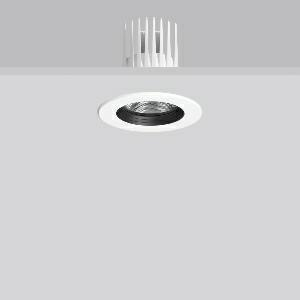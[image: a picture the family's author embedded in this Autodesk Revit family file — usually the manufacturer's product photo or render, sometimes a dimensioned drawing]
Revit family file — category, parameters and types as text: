
# Revit family: heledon_mini_e_901741_002_3_268f
name_source: partatom
category: Lighting Fixtures
units: mm (PartAtom-declared; Revit-internal decimal feet)

## family parameters
Cut with Voids When Loaded = No
Host = Face
Light Source = No
Part Type = Normal
Room Calculation Point = No
Round Connector Dimension = Use Diameter
Shared = No

## types (1)
- HELEDON mini E (1 x LED Modul 935, 2500 lm, 3500)
    Apparent Load = 20 VA
    Approval mark = CE
    CIE Flux Codes = 99 100 100 100 100
    Color Rendering = 92
    Color Temperature = 3500
    Default Elevation = 1800 mm
    Description = Series: HELEDON mini
Round recessed downlight. Housing: die-cast aluminium, powder-coated. Black plastic ring and recessed LED to prevent glare from the side. Optical assembly with reflector made of MIRO-Silver with 98% total light reflection for outstanding efficiency - can be changed without tools. Best colour rendering index Ra>90. Suitable for Recessed ceiling mounting. Installation without tools thanks to spring fastening system. Including separate LED converter with connecting cable 600 mm.High quality converter without flickering and stroboscopic effect. Through-wiring box (5 pole) available as accessory. The following accessories can be mounted without use of tools: interchangeable lenses, decorative glasses, honeycomb louvre, clear and frosted diffusers, white interchangeable plastic ring. 
Colour: traffic white, matt (RAL 9016)
Diameter: 124 mm
Height: 3 mm
Cut-out diameter: 114 mm
Recess height: 170 mm
Luminaire: recess height: 120 mm
Lamp: LED
Socket: without socket
Colour temperature: 3500K
Colour rendering index (CRI): 92
System power: 20 W
Rated luminous flux: 2500 lm
Luminous efficiency: 125 lm/W
Control gear: Regulated power supply
Protection class: II
Type of protection: IP 20
    Height = 0 mm  [stored 0 ft]
    Lamp = 1 x LED Modul 935
    Lamp Light Flux = 2500 lm
    Lamp count = 1
    Length = 124 mm  [stored 0.406824 ft]
    Lifetime = 50000 h
    Luminous efficacy = 125 lm/W
    Manufacturer = RZB
    ModVariant = No
    Model = 901741.002.3
    Mounting Place = Ceiling
    Mounting Type = Recessed
    Number of Poles = 1
    OnlyDefault = Yes
    Power Factor = 1
    Product Name = HELEDON mini E
    Product group = Recessed downlights
    ProductGroupID = 402
    Protection Class = Protection class II
    Protection Degree = IP 20
    RLX_Detail_Level = 1
    RLX_Emergency_Light_Flux = 0 lm
    RLX_Emergency_Type = 0
    RLX_Emergency_Type_DB = No
    RlxData = <blob elided: 125017 chars, md5=462be6a9>
    Socket = socket
    Standby Power = 0 W
    System Light Flux = 2500 lm
    System Power = 20 W
    Type Comments = Product without accessories
    Type Image = 901657.002.jpg
    URL = http://relux.com
    VarID = ---
    Voltage = 230 V
    Voltage Range = 220-240 V
    Weight = 0.00 kg
    Width = 0 mm  [stored 0 ft]

note: [stored X ft] marks values corroborated as IEEE doubles in the binary element streams (Revit-internal decimal feet)

## geometry (parser evidence)
native form markers: Blend x4, Sweep x10
no freeform markers — native parametric forms only
